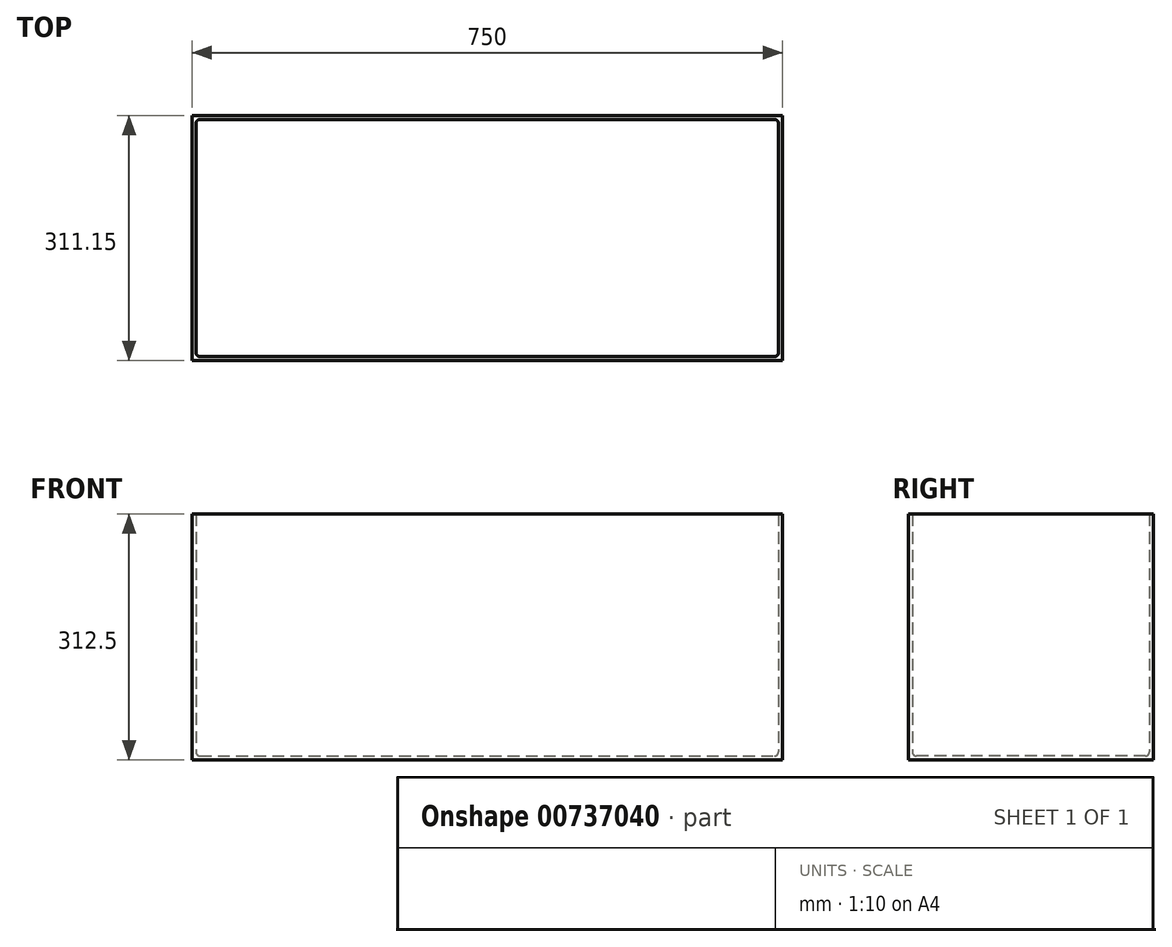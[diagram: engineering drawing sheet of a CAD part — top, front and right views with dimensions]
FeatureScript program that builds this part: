
annotation { "Feature Type Name" : "Feature", "Feature Type Description" : "" }
export const myFeature = defineFeature(function(context is Context, id is Id, definition is map)
    precondition{}
    {
        {
            var Q0;
            Q0=qCreatedBy(makeId("Top.planeOp"),FACE);
            var sketch = newSketch(context, id + "F0", { "sketchPlane" : qUnion([Q0])});
            skLineSegment(sketch, "E0.bottom", {"start": v(0, 311.15) * mm, "end": v(750, 311.15) * mm});
            skLineSegment(sketch, "E0.top", {"start": v(0, 0) * mm, "end": v(750, 0) * mm});
            skLineSegment(sketch, "E0.left", {"start": v(0, 311.15) * mm, "end": v(0, 0) * mm});
            skLineSegment(sketch, "E0.right", {"start": v(750, 311.15) * mm, "end": v(750, 0) * mm});
            skLineSegment(sketch, "E1.0", {"start": v(5, 306.15) * mm, "end": v(745, 306.15) * mm});
            skLineSegment(sketch, "E1.1", {"start": v(5, 306.15) * mm, "end": v(5, 5) * mm});
            skLineSegment(sketch, "E1.2", {"start": v(5, 5) * mm, "end": v(745, 5) * mm});
            skLineSegment(sketch, "E1.3", {"start": v(745, 306.15) * mm, "end": v(745, 5) * mm});
            skSolve(sketch);
        }
        {
            var Q0;
            Q0=makeQuery(id+"F0.imprint","IMPRINT",FACE,{"disambiguationData":[TD([[makeQuery(id+"F0.imprint","IMPRINT",EDGE,{"derivedFrom":sQuery(id+"F0.wireOp",EDGE,"E1.0")}),-1.0]])]});
            extrude(context, id + "F1", {"entities" : qUnion([Q0]), "depth" : 5 * mm, "offsetDistance" : 25 * mm});
        }
        {
            var Q0;
            Q0=makeQuery(id+"F0.imprint","IMPRINT",FACE,{"disambiguationData":[TD([[makeQuery(id+"F0.imprint","IMPRINT",EDGE,{"derivedFrom":sQuery(id+"F0.wireOp",EDGE,"E0.bottom")}),-1.0]])]});
            extrude(context, id + "F2", {"entities" : qUnion([Q0]), "operationType" : NewBodyOperationType.ADD, "depth" : 312.5 * mm, "offsetDistance" : 25 * mm});
        }
        {
            var Q0;
            Q0=makeQuery(id+"F1.opExtrude","CAP_FACE",FACE,{"disambiguationData":[OSD([sQuery(id+"F0.wireOp",EDGE,"E1.0"),sQuery(id+"F0.wireOp",EDGE,"E1.1"),sQuery(id+"F0.wireOp",EDGE,"E1.2"),sQuery(id+"F0.wireOp",EDGE,"E1.3")])],"isStart":false});
            var Q1;
            Q1=makeQuery(id+"F2.opExtrude","SWEPT_EDGE",EDGE,{"disambiguationData":[OSD([sQuery(id+"F0.wireOp",EDGE,"E1.0"),sQuery(id+"F0.wireOp",EDGE,"E1.1")])]});
            var Q2;
            Q2=makeQuery(id+"F2.opExtrude","SWEPT_EDGE",EDGE,{"disambiguationData":[OSD([sQuery(id+"F0.wireOp",EDGE,"E1.1"),sQuery(id+"F0.wireOp",EDGE,"E1.2")])]});
            var Q3;
            Q3=makeQuery(id+"F2.opExtrude","SWEPT_EDGE",EDGE,{"disambiguationData":[OSD([sQuery(id+"F0.wireOp",EDGE,"E1.0"),sQuery(id+"F0.wireOp",EDGE,"E1.3")])]});
            var Q4;
            Q4=makeQuery(id+"F2.opExtrude","SWEPT_EDGE",EDGE,{"disambiguationData":[OSD([sQuery(id+"F0.wireOp",EDGE,"E1.2"),sQuery(id+"F0.wireOp",EDGE,"E1.3")])]});
            fillet(context, id + "F3", {"entities" : qUnion([Q0, Q1, Q2, Q3, Q4]), "tangentPropagation" : true, "radius" : 5 * mm, "defaultsChanged" : false, "vertexSettings" : [], "allowEdgeOverflow" : false});
        }
    });
